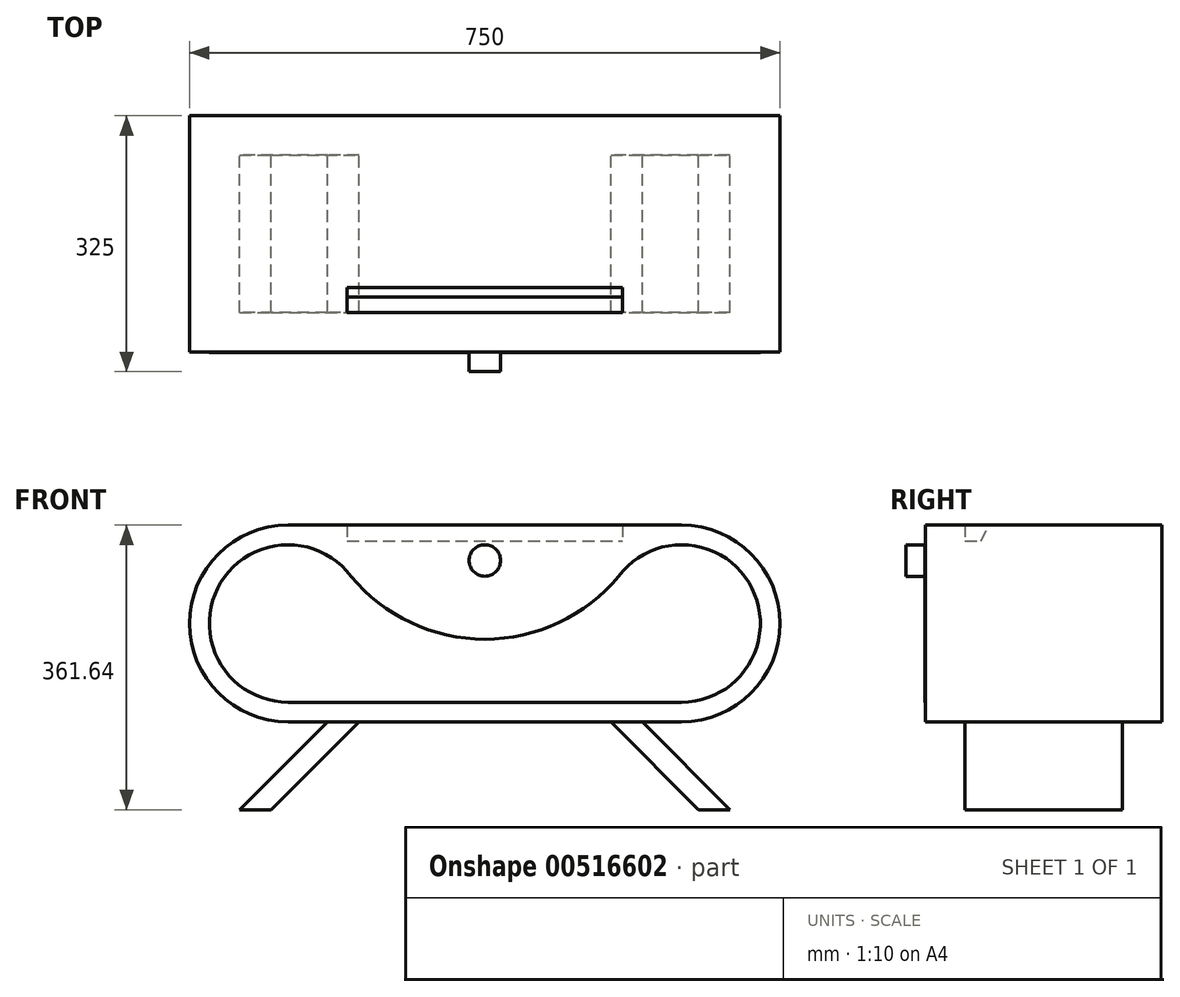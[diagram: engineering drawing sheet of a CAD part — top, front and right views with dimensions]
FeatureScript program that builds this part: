
annotation { "Feature Type Name" : "Feature", "Feature Type Description" : "" }
export const myFeature = defineFeature(function(context is Context, id is Id, definition is map)
    precondition{}
    {
        {
            var Q0;
            Q0=qCreatedBy(makeId("Front.planeOp"),FACE);
            var sketch = newSketch(context, id + "F0", { "sketchPlane" : qUnion([Q0])});
            skLineSegment(sketch, "E0.bottom", {"start": v(0, 0) * mm, "end": v(-500, 0) * mm});
            skLineSegment(sketch, "E0.top", {"start": v(0, 250) * mm, "end": v(-500, 250) * mm});
            skArc(sketch, "E1", {"start": v(0, 0) * mm, "mid": v(125, 125) * mm, "end": v(0, 250) * mm});
            skArc(sketch, "E2", {"start": v(-500, 250) * mm, "mid": v(-625, 125) * mm, "end": v(-500, 0) * mm});
            skSolve(sketch);
        }
        {
            var Q0;
            Q0 = qSketchRegion(id + "F0", true);
            extrude(context, id + "F1", {"entities" : qUnion([Q0]), "endBound" : BoundingType.SYMMETRIC, "depth" : 300 * mm, "offsetDistance" : 25 * mm});
        }
        {
            var Q0;
            Q0=qCreatedBy(makeId("Front.planeOp"),FACE);
            var sketch = newSketch(context, id + "F2", { "sketchPlane" : qUnion([Q0])});
            skLineSegment(sketch, "E3", {"start": v(-50, 0) * mm, "end": v(61.64, -111.64) * mm});
            skLineSegment(sketch, "E4", {"start": v(61.64, -111.64) * mm, "end": v(21.64, -111.64) * mm});
            skLineSegment(sketch, "E5", {"start": v(21.64, -111.64) * mm, "end": v(-90, 0) * mm});
            skLineSegment(sketch, "E6", {"start": v(-90, 0) * mm, "end": v(-50, 0) * mm});
            skSolve(sketch);
        }
        {
            var Q0;
            Q0 = qSketchRegion(id + "F2", true);
            extrude(context, id + "F3", {"entities" : qUnion([Q0]), "operationType" : NewBodyOperationType.ADD, "endBound" : BoundingType.SYMMETRIC, "depth" : 200 * mm, "offsetDistance" : 25 * mm});
        }
        {
            var Q0;
            Q0=qCreatedBy(makeId("Right.planeOp"),FACE);
            cPlane(context, id + "F4", {"entities" : qUnion([Q0]), "cplaneType" : CPlaneType.OFFSET, "offset" : 250 * mm, "oppositeDirection" : true, "width" : 150 * mm, "height" : 150 * mm});
        }
        {
            var Q0;
            Q0=makeQuery(id+"F1.opExtrude","SWEPT_BODY",BODY,{"disambiguationData":[OSD([sQuery(id+"F0.wireOp",EDGE,"E0.bottom"),sQuery(id+"F0.wireOp",EDGE,"E0.top"),sQuery(id+"F0.wireOp",EDGE,"E1"),sQuery(id+"F0.wireOp",EDGE,"E2")])]});
            var Q1;
            Q1=qCreatedBy(id+"F4.planeOp",FACE);
            mirror(context, id + "F5", {"operationType" : NewBodyOperationType.ADD, "entities" : qUnion([Q0]), "mirrorPlane" : qUnion([Q1])});
        }
        {
            var Q0;
            Q0=makeQuery(id+"F1.opExtrude","CAP_FACE",FACE,{"disambiguationData":[OSD([sQuery(id+"F0.wireOp",EDGE,"E0.bottom"),sQuery(id+"F0.wireOp",EDGE,"E0.top"),sQuery(id+"F0.wireOp",EDGE,"E1"),sQuery(id+"F0.wireOp",EDGE,"E2")])],"isStart":false});
            var sketch = newSketch(context, id + "F6", { "sketchPlane" : qUnion([Q0])});
            skCircle(sketch, "E7", {"center": v(-500, 125) * mm, "radius": 100 * mm});
            skCircle(sketch, "E8", {"center": v(0, 125) * mm, "radius": 100 * mm});
            skLineSegment(sketch, "E9", {"start": v(-500, 25) * mm, "end": v(0, 25) * mm});
            skArc(sketch, "E10", {"start": v(-420, 185) * mm, "mid": v(-250, 105) * mm, "end": v(-80, 185) * mm});
            skSolve(sketch);
        }
        {
            var Q0;
            Q0 = qSketchRegion(id + "F6", true);
            extrude(context, id + "F7", {"entities" : qUnion([Q0]), "operationType" : NewBodyOperationType.ADD, "depth" : 1 * mm, "offsetDistance" : 25 * mm});
        }
        {
            var Q0;
            Q0=makeQuery(id+"F1.opExtrude","CAP_FACE",FACE,{"disambiguationData":[OSD([sQuery(id+"F0.wireOp",EDGE,"E0.bottom"),sQuery(id+"F0.wireOp",EDGE,"E0.top"),sQuery(id+"F0.wireOp",EDGE,"E1"),sQuery(id+"F0.wireOp",EDGE,"E2")])],"isStart":false});
            var sketch = newSketch(context, id + "F8", { "sketchPlane" : qUnion([Q0])});
            skCircle(sketch, "E11", {"center": v(-250, 205) * mm, "radius": 20 * mm});
            skPoint(sketch, "E11.centerSnap0", {"position": v(-250, 0) * mm});
            skSolve(sketch);
        }
        {
            var Q0;
            Q0 = qSketchRegion(id + "F8", true);
            extrude(context, id + "F9", {"entities" : qUnion([Q0]), "operationType" : NewBodyOperationType.ADD, "depth" : 25 * mm, "offsetDistance" : 25 * mm});
        }
        {
            var Q0;
            Q0=qCreatedBy(id+"F4.planeOp",FACE);
            var sketch = newSketch(context, id + "F10", { "sketchPlane" : qUnion([Q0])});
            skLineSegment(sketch, "E12", {"start": v(-100, 250.78) * mm, "end": v(-100, 230) * mm});
            skLineSegment(sketch, "E13", {"start": v(-100, 230) * mm, "end": v(-80, 230) * mm});
            skLineSegment(sketch, "E14", {"start": v(-80, 230) * mm, "end": v(-68, 250.78) * mm});
            skLineSegment(sketch, "E15", {"start": v(-100, 250.78) * mm, "end": v(-68, 250.78) * mm});
            skSolve(sketch);
        }
        {
            var Q0;
            Q0 = qSketchRegion(id + "F10", true);
            extrude(context, id + "F11", {"entities" : qUnion([Q0]), "operationType" : NewBodyOperationType.REMOVE, "endBound" : BoundingType.SYMMETRIC, "oppositeDirection" : true, "depth" : 350 * mm, "offsetDistance" : 25 * mm});
        }
    });
